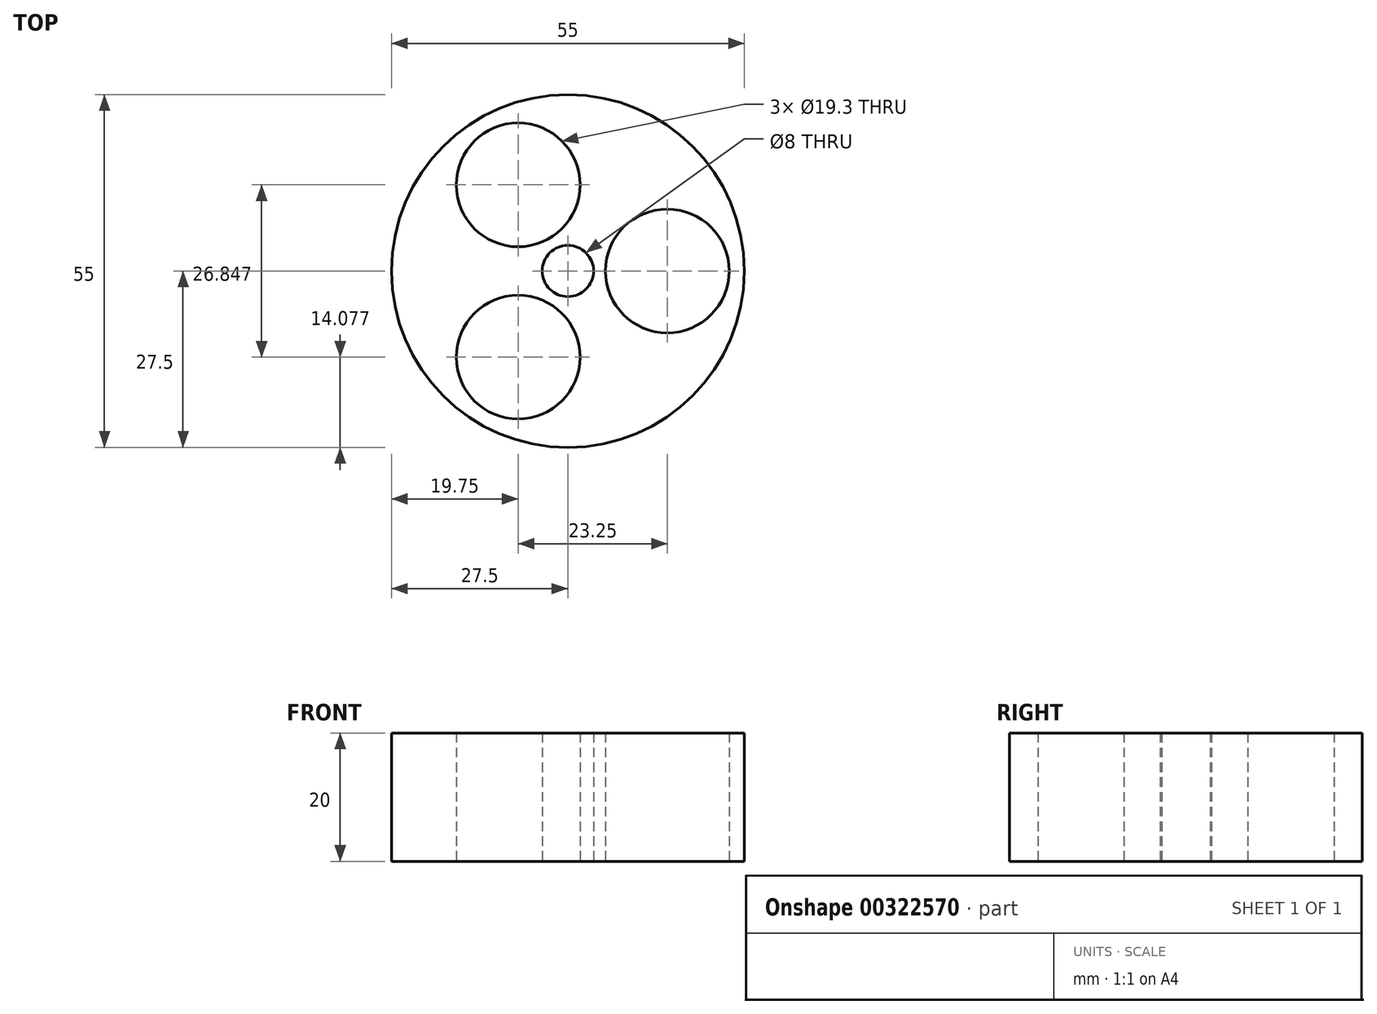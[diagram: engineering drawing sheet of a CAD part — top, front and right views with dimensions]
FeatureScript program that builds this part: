
annotation { "Feature Type Name" : "Feature", "Feature Type Description" : "" }
export const myFeature = defineFeature(function(context is Context, id is Id, definition is map)
    precondition{}
    {
        {
            var Q0;
            Q0=qCreatedBy(makeId("Top.planeOp"),FACE);
            var sketch = newSketch(context, id + "F0", { "sketchPlane" : qUnion([Q0])});
            skCircle(sketch, "E0", {"center": v(0, 0) * mm, "radius": 27.5 * mm});
            skLineSegment(sketch, "E1", {"start": v(0, 0) * mm, "end": v(15.5, 0) * mm, "construction": true});
            skCircle(sketch, "E2", {"center": v(15.5, 0) * mm, "radius": 9.65 * mm});
            skCircle(sketch, "E3.1.0", {"center": v(-7.75, 13.42) * mm, "radius": 9.65 * mm});
            skCircle(sketch, "E3.2.0", {"center": v(-7.75, -13.42) * mm, "radius": 9.65 * mm});
            skCircle(sketch, "E4", {"center": v(0, 0) * mm, "radius": 4 * mm});
            skSolve(sketch);
        }
        {
            var Q0;
            Q0=makeQuery(id+"F0.imprint","IMPRINT",FACE,{"disambiguationData":[TD([[makeQuery(id+"F0.imprint","IMPRINT",EDGE,{"derivedFrom":sQuery(id+"F0.wireOp",EDGE,"E0")}),1.0]])]});
            extrude(context, id + "F1", {"entities" : qUnion([Q0]), "depth" : 20 * mm});
        }
    });
